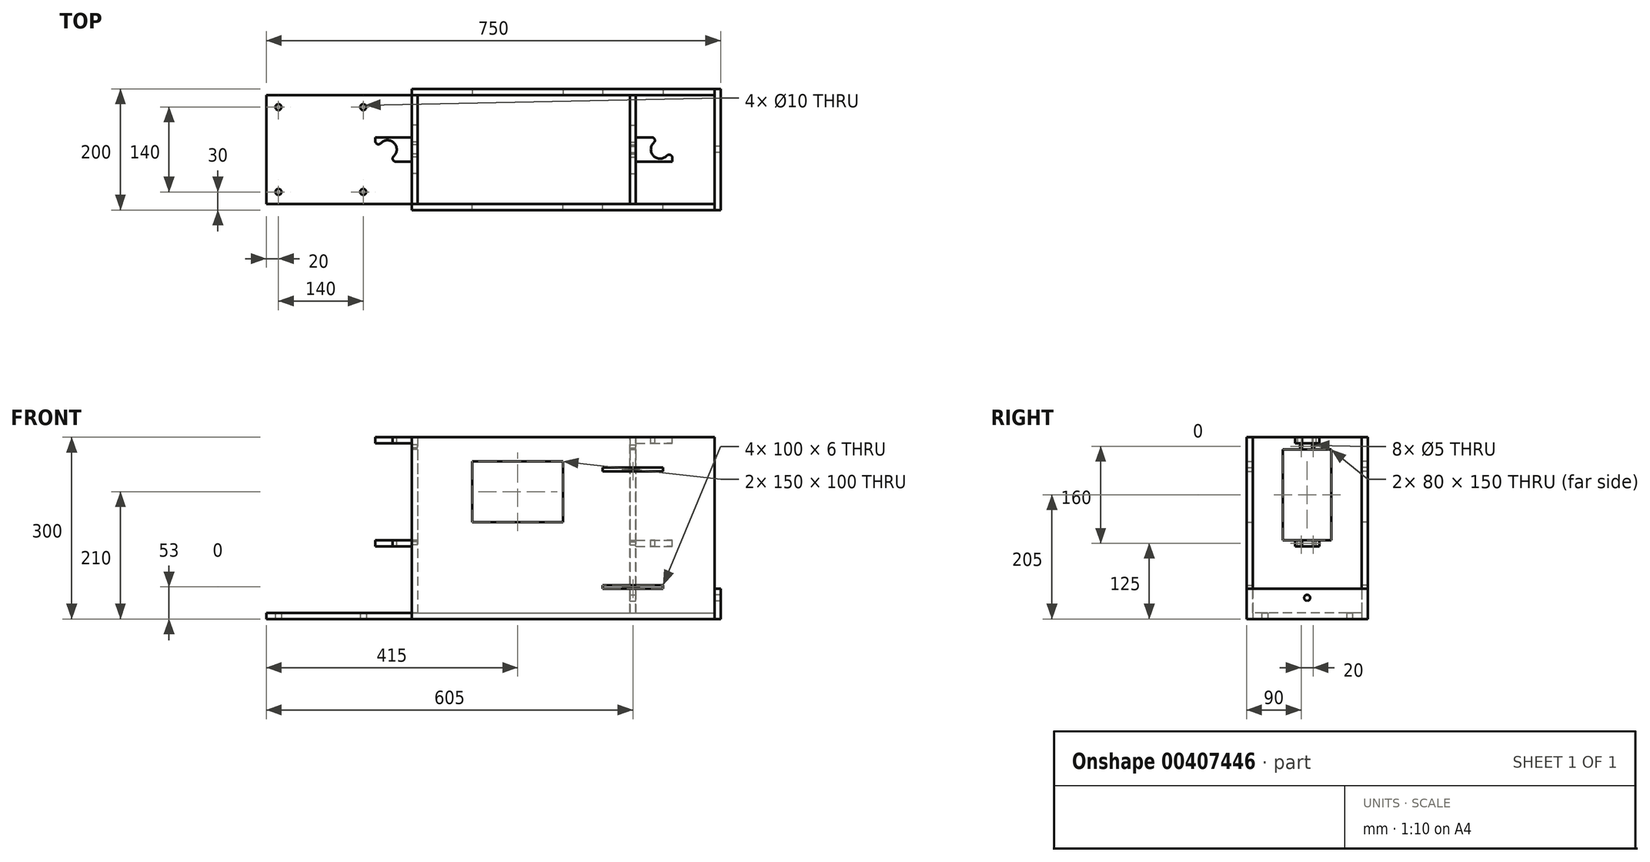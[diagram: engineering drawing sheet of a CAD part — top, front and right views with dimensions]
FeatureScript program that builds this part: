
annotation { "Feature Type Name" : "Feature", "Feature Type Description" : "" }
export const myFeature = defineFeature(function(context is Context, id is Id, definition is map)
    precondition{}
    {
        {
            var Q0;
            Q0=qCreatedBy(makeId("Top.planeOp"),FACE);
            var sketch = newSketch(context, id + "F0", { "sketchPlane" : qUnion([Q0])});
            skLineSegment(sketch, "E0.bottom", {"start": v(-240, 90) * mm, "end": v(500, 90) * mm});
            skLineSegment(sketch, "E0.top", {"start": v(-240, -90) * mm, "end": v(500, -90) * mm});
            skLineSegment(sketch, "E0.left", {"start": v(-240, 90) * mm, "end": v(-240, -90) * mm});
            skLineSegment(sketch, "E0.right", {"start": v(500, 90) * mm, "end": v(500, -90) * mm});
            skCircle(sketch, "E1", {"center": v(-220, 70) * mm, "radius": 5 * mm});
            skCircle(sketch, "E2", {"center": v(-220, -70) * mm, "radius": 5 * mm});
            skCircle(sketch, "E3", {"center": v(-80, 70) * mm, "radius": 5 * mm});
            skCircle(sketch, "E4", {"center": v(-80, -70) * mm, "radius": 5 * mm});
            skSolve(sketch);
        }
        {
            var Q0;
            Q0=makeQuery(id+"F0.imprint","IMPRINT",FACE,{"disambiguationData":[TD([[makeQuery(id+"F0.imprint","IMPRINT",EDGE,{"derivedFrom":sQuery(id+"F0.wireOp",EDGE,"E0.bottom")}),-1.0]])]});
            extrude(context, id + "F1", {"entities" : qUnion([Q0]), "depth" : 10 * mm});
        }
        {
            var Q0;
            Q0=qCreatedBy(makeId("Right.planeOp"),FACE);
            var sketch = newSketch(context, id + "F2", { "sketchPlane" : qUnion([Q0])});
            skLineSegment(sketch, "E5", {"start": v(90, 10) * mm, "end": v(-90, 10) * mm});
            skLineSegment(sketch, "E6", {"start": v(-90, 10) * mm, "end": v(-90, 300) * mm});
            skLineSegment(sketch, "E7", {"start": v(-90, 300) * mm, "end": v(90, 300) * mm});
            skLineSegment(sketch, "E8", {"start": v(90, 300) * mm, "end": v(90, 10) * mm});
            skLineSegment(sketch, "E9.bottom", {"start": v(-40, 280) * mm, "end": v(40, 280) * mm});
            skLineSegment(sketch, "E9.top", {"start": v(-40, 130) * mm, "end": v(40, 130) * mm});
            skLineSegment(sketch, "E9.left", {"start": v(-40, 280) * mm, "end": v(-40, 130) * mm});
            skLineSegment(sketch, "E9.right", {"start": v(40, 280) * mm, "end": v(40, 130) * mm});
            skCircle(sketch, "E10", {"center": v(10, 125) * mm, "radius": 2.5 * mm});
            skCircle(sketch, "E11.MirrorC", {"center": v(-10, 125) * mm, "radius": 2.5 * mm});
            skCircle(sketch, "E12", {"center": v(10, 285) * mm, "radius": 2.5 * mm});
            skCircle(sketch, "E13.MirrorC", {"center": v(-10, 285) * mm, "radius": 2.5 * mm});
            skSolve(sketch);
        }
        {
            var Q0;
            Q0=makeQuery(id+"F2.imprint","IMPRINT",FACE,{"disambiguationData":[TD([[makeQuery(id+"F2.imprint","IMPRINT",EDGE,{"derivedFrom":sQuery(id+"F2.wireOp",EDGE,"E5")}),-1.0]])]});
            extrude(context, id + "F3", {"entities" : qUnion([Q0]), "depth" : 10 * mm});
        }
        {
            var Q0;
            Q0=makeQuery(id+"F3.opExtrude","SWEPT_FACE",FACE,{"disambiguationData":[OSD([sQuery(id+"F2.wireOp",EDGE,"E9.top")])]});
            var sketch = newSketch(context, id + "F4", { "sketchPlane" : qUnion([Q0])});
            skLineSegment(sketch, "E14.bottom", {"start": v(0, -20) * mm, "end": v(-26.43, -20) * mm});
            skLineSegment(sketch, "E14.top", {"start": v(0, 20) * mm, "end": v(-60, 20) * mm});
            skLineSegment(sketch, "E14.left", {"start": v(0, -20) * mm, "end": v(0, 20) * mm});
            skLineSegment(sketch, "E14.right", {"start": v(-60, 13.57) * mm, "end": v(-60, 20) * mm});
            skArc(sketch, "E15", {"start": v(-29.25, -10.75) * mm, "mid": v(-29.25, 10.75) * mm, "end": v(-50.75, 10.75) * mm});
            skPoint(sketch, "E15.centerSnap0", {"position": v(-60, 0) * mm});
            skPoint(sketch, "E15.centerSnap1", {"position": v(-30, -20) * mm});
            skLineSegment(sketch, "E16", {"start": v(-29.25, -10.75) * mm, "end": v(-29.97, -11.46) * mm});
            skLineSegment(sketch, "E17", {"start": v(-50.75, 10.75) * mm, "end": v(-51.46, 10.03) * mm});
            skPoint(sketch, "E18.orphan", {"position": v(-60, -20) * mm});
            skPoint(sketch, "E19.visualSharp", {"position": v(-38.5, -20) * mm});
            skArc(sketch, "E19.filletArc", {"start": v(-29.97, -11.46) * mm, "mid": v(-31.05, -16.91) * mm, "end": v(-26.43, -20) * mm});
            skPoint(sketch, "E20.visualSharp", {"position": v(-60, 1.5) * mm});
            skArc(sketch, "E20.filletArc", {"start": v(-60, 13.57) * mm, "mid": v(-56.91, 8.95) * mm, "end": v(-51.46, 10.03) * mm});
            skSolve(sketch);
        }
        {
            var Q0;
            Q0=makeQuery(id+"F4.imprint","IMPRINT",FACE,{"disambiguationData":[TD([[makeQuery(id+"F4.imprint","IMPRINT",EDGE,{"derivedFrom":sQuery(id+"F4.wireOp",EDGE,"E14.bottom")}),-1.0]])]});
            extrude(context, id + "F5", {"entities" : qUnion([Q0]), "oppositeDirection" : true, "depth" : 10 * mm});
        }
        {
            var Q0;
            Q0=makeQuery(id+"F5.opExtrude","SWEPT_BODY",BODY,{"disambiguationData":[OSD([sQuery(id+"F4.wireOp",EDGE,"E14.bottom"),sQuery(id+"F4.wireOp",EDGE,"E14.top"),sQuery(id+"F4.wireOp",EDGE,"E14.left"),sQuery(id+"F4.wireOp",EDGE,"E14.right"),sQuery(id+"F4.wireOp",EDGE,"E15"),sQuery(id+"F4.wireOp",EDGE,"E16"),sQuery(id+"F4.wireOp",EDGE,"E17"),sQuery(id+"F4.wireOp",EDGE,"E19.filletArc"),sQuery(id+"F4.wireOp",EDGE,"E20.filletArc")])]});
            transform(context, id + "F6", {"entities" : qUnion([Q0]), "transformType" : TransformType.TRANSLATION_3D, "dx" : 0 * mm, "dy" : 0 * mm, "dz" : 170 * mm, "makeCopy" : true});
        }
        {
            var Q0;
            Q0=makeQuery(id+"F3.opExtrude","CAP_FACE",FACE,{"disambiguationData":[OSD([sQuery(id+"F2.wireOp",EDGE,"E5"),sQuery(id+"F2.wireOp",EDGE,"E6"),sQuery(id+"F2.wireOp",EDGE,"E7"),sQuery(id+"F2.wireOp",EDGE,"E8"),sQuery(id+"F2.wireOp",EDGE,"E9.bottom"),sQuery(id+"F2.wireOp",EDGE,"E9.top"),sQuery(id+"F2.wireOp",EDGE,"E9.left"),sQuery(id+"F2.wireOp",EDGE,"E9.right"),sQuery(id+"F2.wireOp",EDGE,"E10"),sQuery(id+"F2.wireOp",EDGE,"E11.MirrorC"),sQuery(id+"F2.wireOp",EDGE,"E12"),sQuery(id+"F2.wireOp",EDGE,"E13.MirrorC")])],"isStart":false});
            cPlane(context, id + "F7", {"entities" : qUnion([Q0]), "cplaneType" : CPlaneType.OFFSET, "offset" : 360 * mm, "width" : 150 * mm, "height" : 150 * mm});
        }
        {
            var Q0;
            Q0=qCreatedBy(id+"F7.planeOp",FACE);
            var sketch = newSketch(context, id + "F8", { "sketchPlane" : qUnion([Q0])});
            skLineSegment(sketch, "E21", {"start": v(90, 10) * mm, "end": v(-90, 10) * mm});
            skLineSegment(sketch, "E22", {"start": v(-90, 10) * mm, "end": v(-90, 300) * mm});
            skLineSegment(sketch, "E23", {"start": v(-90, 300) * mm, "end": v(90, 300) * mm});
            skLineSegment(sketch, "E24", {"start": v(90, 300) * mm, "end": v(90, 10) * mm});
            skLineSegment(sketch, "E25.bottom", {"start": v(-40, 280) * mm, "end": v(40, 280) * mm});
            skLineSegment(sketch, "E25.top", {"start": v(-40, 130) * mm, "end": v(40, 130) * mm});
            skLineSegment(sketch, "E25.left", {"start": v(-40, 280) * mm, "end": v(-40, 130) * mm});
            skLineSegment(sketch, "E25.right", {"start": v(40, 280) * mm, "end": v(40, 130) * mm});
            skCircle(sketch, "E26", {"center": v(10, 125) * mm, "radius": 2.5 * mm});
            skCircle(sketch, "E27.MirrorC", {"center": v(-10, 125) * mm, "radius": 2.5 * mm});
            skCircle(sketch, "E28", {"center": v(10, 285) * mm, "radius": 2.5 * mm});
            skCircle(sketch, "E29.MirrorC", {"center": v(-10, 285) * mm, "radius": 2.5 * mm});
            skCircle(sketch, "E30", {"center": v(0, 35) * mm, "radius": 5 * mm});
            skSolve(sketch);
        }
        {
            var Q0;
            Q0=makeQuery(id+"F8.imprint","IMPRINT",FACE,{"disambiguationData":[TD([[makeQuery(id+"F8.imprint","IMPRINT",EDGE,{"derivedFrom":sQuery(id+"F8.wireOp",EDGE,"E21")}),-1.0]])]});
            extrude(context, id + "F9", {"entities" : qUnion([Q0]), "oppositeDirection" : true, "depth" : 10 * mm});
        }
        {
            var Q0;
            Q0=makeQuery(id+"F5.opExtrude","SWEPT_BODY",BODY,{"disambiguationData":[OSD([sQuery(id+"F4.wireOp",EDGE,"E14.bottom"),sQuery(id+"F4.wireOp",EDGE,"E14.top"),sQuery(id+"F4.wireOp",EDGE,"E14.left"),sQuery(id+"F4.wireOp",EDGE,"E14.right"),sQuery(id+"F4.wireOp",EDGE,"E15"),sQuery(id+"F4.wireOp",EDGE,"E16"),sQuery(id+"F4.wireOp",EDGE,"E17"),sQuery(id+"F4.wireOp",EDGE,"E19.filletArc"),sQuery(id+"F4.wireOp",EDGE,"E20.filletArc")])]});
            var Q1;
            Q1=makeQuery(id+"F3.opExtrude","CAP_EDGE",EDGE,{"disambiguationData":[OSD([sQuery(id+"F2.wireOp",EDGE,"E9.right")])],"isStart":true});
            transform(context, id + "F10", {"entities" : qUnion([Q0]), "transformType" : TransformType.ROTATION, "transformAxis" : qUnion([Q1]), "angle" : 180 * degree, "makeCopy" : true});
        }
        {
            var Q0;
            Q0=makeQuery(id+"F10.opPattern","COPY",BODY,{"derivedFrom":makeQuery(id+"F5.opExtrude","SWEPT_BODY",BODY,{"disambiguationData":[OSD([sQuery(id+"F4.wireOp",EDGE,"E14.bottom"),sQuery(id+"F4.wireOp",EDGE,"E14.top"),sQuery(id+"F4.wireOp",EDGE,"E14.left"),sQuery(id+"F4.wireOp",EDGE,"E14.right"),sQuery(id+"F4.wireOp",EDGE,"E15"),sQuery(id+"F4.wireOp",EDGE,"E16"),sQuery(id+"F4.wireOp",EDGE,"E17"),sQuery(id+"F4.wireOp",EDGE,"E19.filletArc"),sQuery(id+"F4.wireOp",EDGE,"E20.filletArc")])]}),"instanceName":"1"});
            transform(context, id + "F11", {"entities" : qUnion([Q0]), "transformType" : TransformType.TRANSLATION_3D, "dx" : 370 * mm, "dy" : -80 * mm, "dz" : 0 * mm, "makeCopy" : false});
        }
        {
            var Q0;
            Q0=makeQuery(id+"F10.opPattern","COPY",BODY,{"derivedFrom":makeQuery(id+"F5.opExtrude","SWEPT_BODY",BODY,{"disambiguationData":[OSD([sQuery(id+"F4.wireOp",EDGE,"E14.bottom"),sQuery(id+"F4.wireOp",EDGE,"E14.top"),sQuery(id+"F4.wireOp",EDGE,"E14.left"),sQuery(id+"F4.wireOp",EDGE,"E14.right"),sQuery(id+"F4.wireOp",EDGE,"E15"),sQuery(id+"F4.wireOp",EDGE,"E16"),sQuery(id+"F4.wireOp",EDGE,"E17"),sQuery(id+"F4.wireOp",EDGE,"E19.filletArc"),sQuery(id+"F4.wireOp",EDGE,"E20.filletArc")])]}),"instanceName":"1"});
            transform(context, id + "F12", {"entities" : qUnion([Q0]), "transformType" : TransformType.TRANSLATION_3D, "dx" : 0 * mm, "dy" : 0 * mm, "dz" : 170 * mm, "makeCopy" : true});
        }
        {
            var Q0;
            Q0=makeQuery(id+"F9.boolean.opBoolean","MERGE",FACE,{"derivedFrom":[makeQuery(id+"F3.boolean.opBoolean","MERGE",FACE,{"derivedFrom":[makeQuery(id+"F1.opExtrude","SWEPT_FACE",FACE,{"disambiguationData":[OSD([sQuery(id+"F0.wireOp",EDGE,"E0.top")])]}),makeQuery(id+"F3.opExtrude","SWEPT_FACE",FACE,{"disambiguationData":[OSD([sQuery(id+"F2.wireOp",EDGE,"E6")])]})]}),makeQuery(id+"F9.opExtrude","SWEPT_FACE",FACE,{"disambiguationData":[OSD([sQuery(id+"F8.wireOp",EDGE,"E22")])]})]});
            var sketch = newSketch(context, id + "F13", { "sketchPlane" : qUnion([Q0])});
            skLineSegment(sketch, "E31.bottom", {"start": v(0, 300) * mm, "end": v(500, 300) * mm});
            skLineSegment(sketch, "E31.top", {"start": v(0, 0) * mm, "end": v(500, 0) * mm});
            skLineSegment(sketch, "E31.left", {"start": v(0, 300) * mm, "end": v(0, 0) * mm});
            skLineSegment(sketch, "E31.right", {"start": v(500, 300) * mm, "end": v(500, 0) * mm});
            skLineSegment(sketch, "E32.bottom", {"start": v(100, 260) * mm, "end": v(250, 260) * mm});
            skLineSegment(sketch, "E32.top", {"start": v(100, 160) * mm, "end": v(250, 160) * mm});
            skLineSegment(sketch, "E32.left", {"start": v(100, 260) * mm, "end": v(100, 160) * mm});
            skLineSegment(sketch, "E32.right", {"start": v(250, 260) * mm, "end": v(250, 160) * mm});
            skLineSegment(sketch, "E33.bottom", {"start": v(315, 56) * mm, "end": v(415, 56) * mm});
            skLineSegment(sketch, "E33.top", {"start": v(315, 50) * mm, "end": v(415, 50) * mm});
            skLineSegment(sketch, "E33.left", {"start": v(315, 56) * mm, "end": v(315, 50) * mm});
            skLineSegment(sketch, "E33.right", {"start": v(415, 56) * mm, "end": v(415, 50) * mm});
            skLineSegment(sketch, "E34.bottom", {"start": v(315, 250) * mm, "end": v(415, 250) * mm});
            skLineSegment(sketch, "E34.top", {"start": v(315, 244) * mm, "end": v(415, 244) * mm});
            skLineSegment(sketch, "E34.left", {"start": v(315, 250) * mm, "end": v(315, 244) * mm});
            skLineSegment(sketch, "E34.right", {"start": v(415, 250) * mm, "end": v(415, 244) * mm});
            skSolve(sketch);
        }
        {
            var Q0;
            Q0 = qSketchRegion(id + "F13", true);
            extrude(context, id + "F14", {"entities" : qUnion([Q0]), "depth" : 10 * mm});
        }
        {
            var Q0;
            Q0=makeQuery(id+"F14.opExtrude","SWEPT_BODY",BODY,{"disambiguationData":[OSD([sQuery(id+"F13.wireOp",EDGE,"E31.bottom"),sQuery(id+"F13.wireOp",EDGE,"E31.top"),sQuery(id+"F13.wireOp",EDGE,"E31.left"),sQuery(id+"F13.wireOp",EDGE,"E31.right"),sQuery(id+"F13.wireOp",EDGE,"E32.bottom"),sQuery(id+"F13.wireOp",EDGE,"E32.top"),sQuery(id+"F13.wireOp",EDGE,"E32.left"),sQuery(id+"F13.wireOp",EDGE,"E32.right"),sQuery(id+"F13.wireOp",EDGE,"E33.bottom"),sQuery(id+"F13.wireOp",EDGE,"E33.top"),sQuery(id+"F13.wireOp",EDGE,"E33.left"),sQuery(id+"F13.wireOp",EDGE,"E33.right"),sQuery(id+"F13.wireOp",EDGE,"E34.bottom"),sQuery(id+"F13.wireOp",EDGE,"E34.top"),sQuery(id+"F13.wireOp",EDGE,"E34.left"),sQuery(id+"F13.wireOp",EDGE,"E34.right")])]});
            var Q1;
            Q1=qCreatedBy(makeId("Front.planeOp"),FACE);
            mirror(context, id + "F15", {"entities" : qUnion([Q0]), "mirrorPlane" : qUnion([Q1])});
        }
        {
            var Q0;
            Q0=makeQuery(id+"F14.boolean.opBoolean","MERGE",FACE,{"derivedFrom":[makeQuery(id+"F1.opExtrude","SWEPT_FACE",FACE,{"disambiguationData":[OSD([sQuery(id+"F0.wireOp",EDGE,"E0.right")])]}),makeQuery(id+"F14.opExtrude","SWEPT_FACE",FACE,{"disambiguationData":[OSD([sQuery(id+"F13.wireOp",EDGE,"E31.right")])]})]});
            var sketch = newSketch(context, id + "F16", { "sketchPlane" : qUnion([Q0])});
            skLineSegment(sketch, "E35.bottom", {"start": v(-100, 50) * mm, "end": v(100, 50) * mm});
            skLineSegment(sketch, "E35.top", {"start": v(-100, 0) * mm, "end": v(100, 0) * mm});
            skLineSegment(sketch, "E35.left", {"start": v(-100, 50) * mm, "end": v(-100, 0) * mm});
            skLineSegment(sketch, "E35.right", {"start": v(100, 50) * mm, "end": v(100, 0) * mm});
            skCircle(sketch, "E36", {"center": v(0, 35) * mm, "radius": 5 * mm});
            skSolve(sketch);
        }
        {
            var Q0;
            Q0 = qSketchRegion(id + "F16", true);
            extrude(context, id + "F17", {"entities" : qUnion([Q0]), "depth" : 10 * mm});
        }
    });
